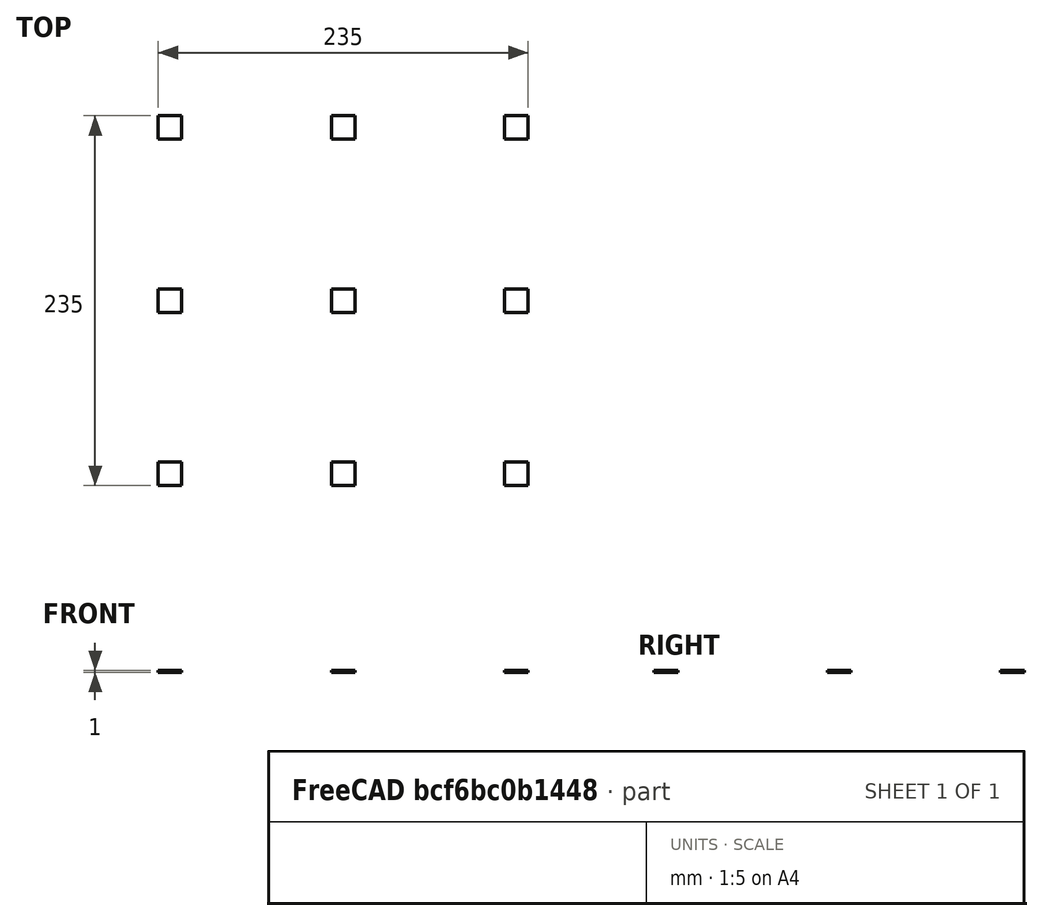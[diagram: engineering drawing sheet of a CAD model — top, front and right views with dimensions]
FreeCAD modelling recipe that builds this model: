
FCSTD DOCUMENT  (FreeCAD 0.19R)
Label: MeshTest
License: All rights reserved
LicenseURL: http://en.wikipedia.org/wiki/All_rights_reserved
objects: Part::Box×9, Part::MultiFuse×1, Mesh::Feature×1
note: 10 computed .brp shape members not serialized (recipe doc carries the construction recipe); baked Part::Feature solids carry a one-line shape summary decoded from their .brp

FEATURE [Part::Box] Box  label="Cube"
  AttacherType = Attacher::AttachEngine3D
  Height = 1
  Length = 15
  Width = 15
FEATURE [Part::Box] Box001  label="Cube001"
  AttacherType = Attacher::AttachEngine3D
  Height = 1
  Length = 15
  Placement = pos=(110,0,0) rot=(0,0,1;0rad)
  Width = 15
FEATURE [Part::Box] Box002  label="Cube002"
  AttacherType = Attacher::AttachEngine3D
  Height = 1
  Length = 15
  Placement = pos=(-110,0,0) rot=(0,0,1;0rad)
  Width = 15
FEATURE [Part::Box] Box003  label="Cube003"
  AttacherType = Attacher::AttachEngine3D
  Height = 1
  Length = 15
  Placement = pos=(0,110,0) rot=(0,0,1;0rad)
  Width = 15
FEATURE [Part::Box] Box004  label="Cube004"
  AttacherType = Attacher::AttachEngine3D
  Height = 1
  Length = 15
  Placement = pos=(0,-110,0) rot=(0,0,1;0rad)
  Width = 15
FEATURE [Part::Box] Box005  label="Cube005"
  AttacherType = Attacher::AttachEngine3D
  Height = 1
  Length = 15
  Placement = pos=(110,-110,0) rot=(0,0,1;0rad)
  Width = 15
FEATURE [Part::Box] Box006  label="Cube006"
  AttacherType = Attacher::AttachEngine3D
  Height = 1
  Length = 15
  Placement = pos=(110,110,0) rot=(0,0,1;0rad)
  Width = 15
FEATURE [Part::Box] Box007  label="Cube007"
  AttacherType = Attacher::AttachEngine3D
  Height = 1
  Length = 15
  Placement = pos=(-110,110,0) rot=(0,0,1;0rad)
  Width = 15
FEATURE [Part::Box] Box008  label="Cube008"
  AttacherType = Attacher::AttachEngine3D
  Height = 1
  Length = 15
  Placement = pos=(-110,-110,0) rot=(0,0,1;0rad)
  Width = 15
FEATURE [Part::MultiFuse] Fusion
  Shapes = -> [Box,Box001,Box002,Box003,Box004,Box005,Box006,Box007,Box008]
FEATURE [Mesh::Feature] Mesh  label="Fusion (Meshed)"
